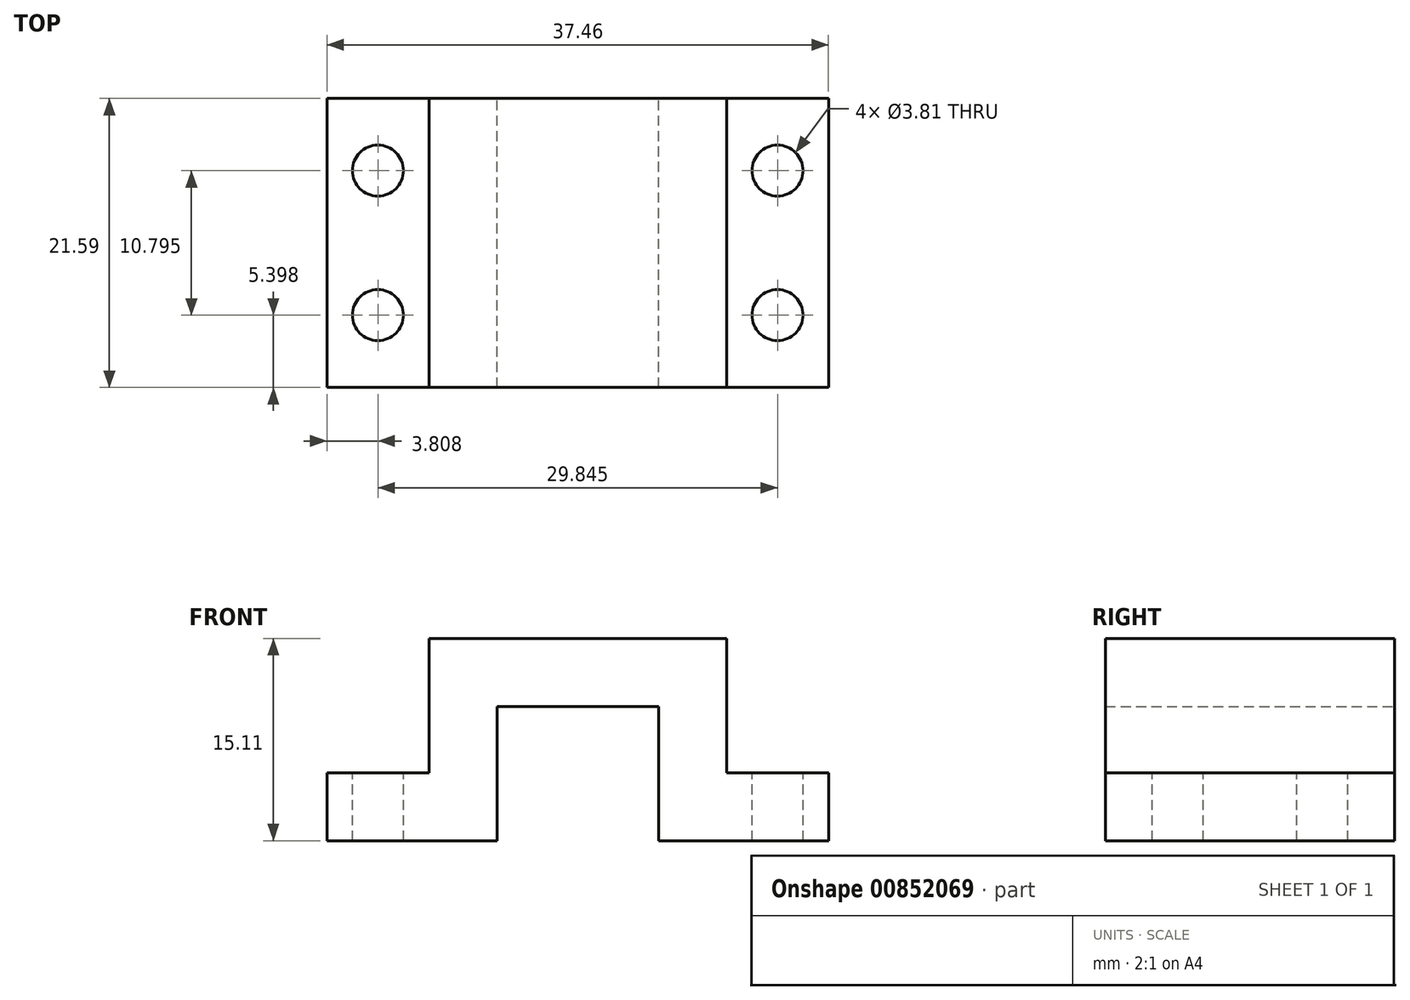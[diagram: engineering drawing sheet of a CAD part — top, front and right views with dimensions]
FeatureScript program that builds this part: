
annotation { "Feature Type Name" : "Feature", "Feature Type Description" : "" }
export const myFeature = defineFeature(function(context is Context, id is Id, definition is map)
    precondition{}
    {
        {
            var Q0;
            Q0=qCreatedBy(makeId("Front.planeOp"),FACE);
            var sketch = newSketch(context, id + "F0", { "sketchPlane" : qUnion([Q0])});
            skLineSegment(sketch, "E0", {"start": v(-18.73, 0) * mm, "end": v(-6.03, 0) * mm});
            skLineSegment(sketch, "E1", {"start": v(-6.03, 0) * mm, "end": v(-6.03, 10.03) * mm});
            skLineSegment(sketch, "E2", {"start": v(-6.03, 10.03) * mm, "end": v(0, 10.03) * mm});
            skLineSegment(sketch, "E3", {"start": v(0, 10.03) * mm, "end": v(0, 15.11) * mm, "construction": true});
            skLineSegment(sketch, "E4", {"start": v(0, 15.11) * mm, "end": v(-11.11, 15.11) * mm});
            skLineSegment(sketch, "E5", {"start": v(-11.11, 15.11) * mm, "end": v(-11.11, 5.08) * mm});
            skLineSegment(sketch, "E6", {"start": v(-11.11, 5.08) * mm, "end": v(-18.73, 5.08) * mm});
            skLineSegment(sketch, "E7", {"start": v(-18.73, 5.08) * mm, "end": v(-18.73, 0) * mm});
            skLineSegment(sketch, "E8.MirrorCS", {"start": v(18.73, 5.08) * mm, "end": v(18.73, 0) * mm});
            skLineSegment(sketch, "E9.MirrorCS", {"start": v(11.11, 5.08) * mm, "end": v(18.73, 5.08) * mm});
            skLineSegment(sketch, "E10.MirrorCS", {"start": v(18.73, 0) * mm, "end": v(6.03, 0) * mm});
            skLineSegment(sketch, "E11.MirrorCS", {"start": v(6.03, 10.03) * mm, "end": v(0, 10.03) * mm});
            skLineSegment(sketch, "E12.MirrorCS", {"start": v(0, 15.11) * mm, "end": v(11.11, 15.11) * mm});
            skLineSegment(sketch, "E13.MirrorCS", {"start": v(11.11, 15.11) * mm, "end": v(11.11, 5.08) * mm});
            skLineSegment(sketch, "E14.MirrorCS", {"start": v(6.03, 0) * mm, "end": v(6.03, 10.03) * mm});
            skSolve(sketch);
        }
        {
            var Q0;
            Q0 = qSketchRegion(id + "F0", true);
            extrude(context, id + "F1", {"entities" : qUnion([Q0]), "depth" : 21.59 * mm, "offsetDistance" : 25.4 * mm});
        }
        {
            var Q0;
            Q0=makeQuery(id+"F1.opExtrude","SWEPT_FACE",FACE,{"disambiguationData":[OSD([sQuery(id+"F0.wireOp",EDGE,"E6")])]});
            var sketch = newSketch(context, id + "F2", { "sketchPlane" : qUnion([Q0])});
            skLineSegment(sketch, "E15", {"start": v(-14.92, 0) * mm, "end": v(-14.92, -10.8) * mm, "construction": true});
            skLineSegment(sketch, "E16", {"start": v(0, 0) * mm, "end": v(0, -21.59) * mm, "construction": true});
            skCircle(sketch, "E17", {"center": v(-14.92, -5.4) * mm, "radius": 1.9 * mm});
            skLineSegment(sketch, "E18", {"start": v(-18.73, -10.8) * mm, "end": v(0, -10.8) * mm, "construction": true});
            skLineSegment(sketch, "E19", {"start": v(-14.92, -10.8) * mm, "end": v(-14.92, -21.59) * mm, "construction": true});
            skCircle(sketch, "E20.MirrorC", {"center": v(-14.92, -16.2) * mm, "radius": 1.9 * mm});
            skCircle(sketch, "E21.MirrorC", {"center": v(14.92, -16.2) * mm, "radius": 1.9 * mm});
            skCircle(sketch, "E22.MirrorC", {"center": v(14.92, -5.4) * mm, "radius": 1.9 * mm});
            skSolve(sketch);
        }
        {
            var Q0;
            Q0 = qSketchRegion(id + "F2", true);
            extrude(context, id + "F3", {"entities" : qUnion([Q0]), "operationType" : NewBodyOperationType.REMOVE, "endBound" : BoundingType.THROUGH_ALL, "oppositeDirection" : true, "depth" : 25.4 * mm, "offsetDistance" : 25.4 * mm});
        }
    });
